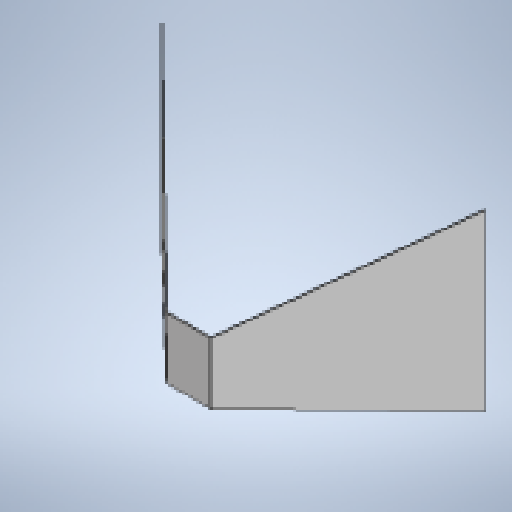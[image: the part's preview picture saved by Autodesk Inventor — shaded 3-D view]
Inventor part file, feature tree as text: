
AUTODESK INVENTOR PART (.ipt)
format: ipt  version: 2025 (Build 290162010, 162A)  size: 303,616 bytes
history: native  units: mm
features: other x4, sheet_metal_op x3, sketch x3, extrude x1, mirror x1, projected_geometry x1
ambient origin geometry x8: Origin, YZ Plane, XZ Plane, XY Plane, X Axis, Y Axis, Z Axis, Center Point
bodies: Solid1 (feature_tree)
feature tree (13):
  sheet_metal_op  "Contour Flange1"
  extrude  "Extrusion3"  Depth=3.0mm
  mirror  "Mirror3"
  other  "A-Side Definition"
  other  "Mark2"
  sketch  "Sketch1"  dims[d7=3.0mm d8=3.0mm]
  other  "Plate1"
  sheet_metal_op  "Bend1"
  sheet_metal_op  "Corner1"
  sketch  "Sketch7"  dims[d9=1.5mm]
  projected_geometry  "Projected Loop2"
  sketch  "Sketch8"  dims[d10=6.0mm d11=3.0mm d12=800.0mm d13=3.0mm d14=3.0mm d15=12.0mm d16=3.0mm d17=3.0mm d38=6.0mm d39=3.0mm d40=3.0mm d44=3.0mm d73=6.0mm d74=742.222353mm d75=23.736478mm d77=3.0mm d78=3.0mm d82=887.0mm d84=6.981317mm d85=0.0mm d86=0.0mm d88=100.0mm]
  other  "Definition1"
